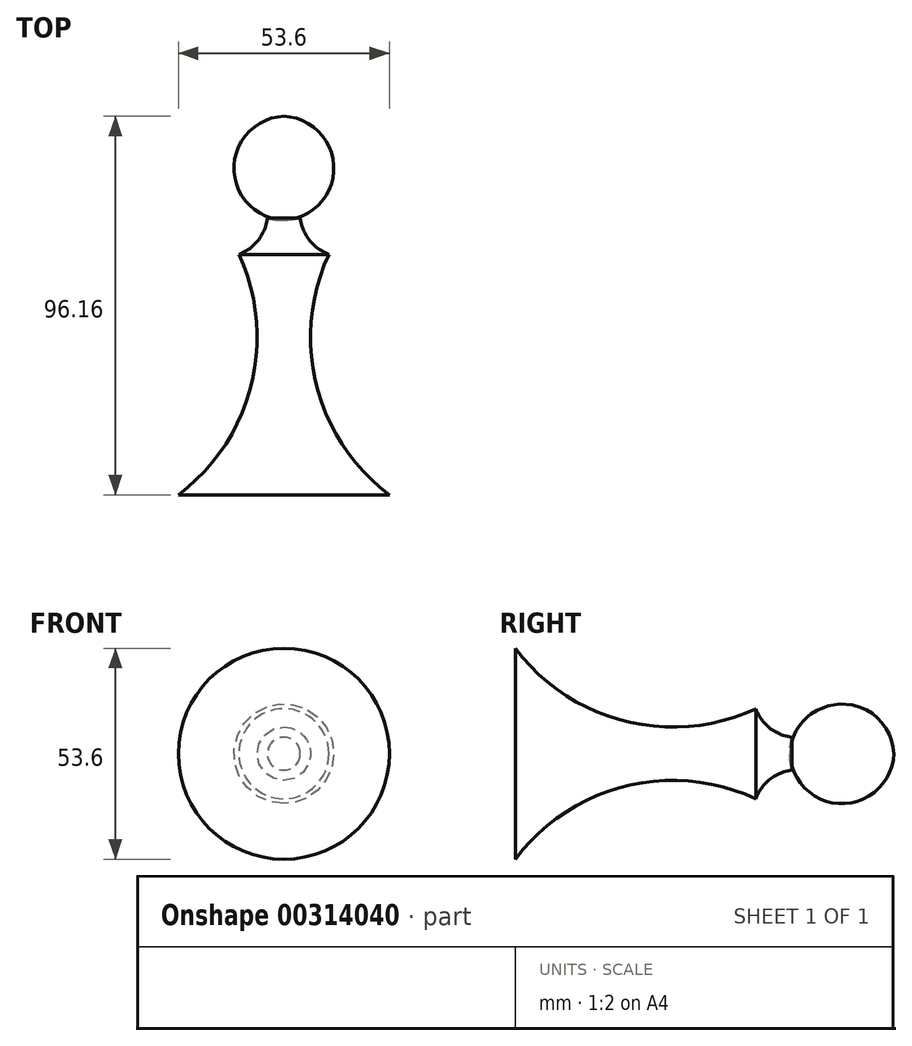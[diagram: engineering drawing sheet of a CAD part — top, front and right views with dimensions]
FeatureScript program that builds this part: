
annotation { "Feature Type Name" : "Feature", "Feature Type Description" : "" }
export const myFeature = defineFeature(function(context is Context, id is Id, definition is map)
    precondition{}
    {
        {
            var Q0;
            Q0=qCreatedBy(makeId("Top.planeOp"),FACE);
            var sketch = newSketch(context, id + "F0", { "sketchPlane" : qUnion([Q0])});
            skLineSegment(sketch, "E0", {"start": v(0, 48.08) * mm, "end": v(0, -48.08) * mm});
            skArc(sketch, "E1", {"start": v(0, 21.68) * mm, "mid": v(13.75, 34.88) * mm, "end": v(0, 48.08) * mm});
            skArc(sketch, "E2", {"start": v(4.17, 22.18) * mm, "mid": v(6.52, 16.58) * mm, "end": v(11.43, 13) * mm});
            skArc(sketch, "E3", {"start": v(11.43, 13) * mm, "mid": v(8.3, -20.26) * mm, "end": v(26.8, -48.08) * mm});
            skLineSegment(sketch, "E4", {"start": v(0, -48.08) * mm, "end": v(26.8, -48.08) * mm});
            skSolve(sketch);
        }
        {
            var Q0;
            {var subQ0=sQuery(id+"F0.wireOp",EDGE,"E1");var subQ1=sQuery(id+"F0.wireOp",EDGE,"E0");var subQ2=makeQuery(id+"F0.imprint","INTERSECT",VERTEX,{"disambiguationData":[OD(0.0)],"derivedFrom":[subQ1,subQ0]});Q0=makeQuery(id+"F0.imprint","IMPRINT",FACE,{"disambiguationData":[TD([[makeQuery(id+"F0.imprint","IMPRINT",EDGE,{"disambiguationData":[TD([[subQ2,-1.0]])],"derivedFrom":subQ1}),1.0]])]});}
            var Q1;
            {var subQ0=sQuery(id+"F0.wireOp",EDGE,"E2");Q1=makeQuery(id+"F0.imprint","IMPRINT",FACE,{"disambiguationData":[TD([[makeQuery(id+"F0.imprint","IMPRINT",EDGE,{"derivedFrom":subQ0}),-1.0]])]});}
            var Q2;
            Q2=sQuery(id+"F0.wireOp",EDGE,"E0");
            revolve(context, id + "F1", {"entities" : qUnion([Q0, Q1]), "axis" : qUnion([Q2]), "revolveType" : RevolveType.FULL});
        }
    });
